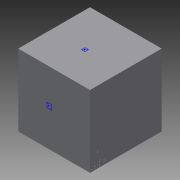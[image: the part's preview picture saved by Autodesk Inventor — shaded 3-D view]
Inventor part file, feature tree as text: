
AUTODESK INVENTOR PART (.ipt)
format: ipt  version: 2014 (Build 180170000, 170)  size: 649,728 bytes
history: native  units: mm
features: sketch x56, extrude x53, other x51
ambient origin geometry x8: Origin, YZ Plane, XZ Plane, XY Plane, X Axis, Y Axis, Z Axis, Center Point
bodies: 实体1 (feature_tree)
feature tree (160):
  extrude  "拉伸1"  Depth=200.0mm
  other  "UCS1"
  other  "UCS2"
  other  "UCS3"
  other  "UCS4"
  other  "UCS5"
  other  "UCS6"
  extrude  "拉伸2"  Depth=43.0mm
  extrude  "拉伸3"  Depth=4.25mm
  extrude  "拉伸4"  Depth=15.5mm
  extrude  "拉伸5"  TaperAngle=0.0deg  [1 undecoded]
  extrude  "拉伸6"  Depth=0.75mm
  extrude  "拉伸7"  Depth=31.75mm
  extrude  "拉伸8"  Depth=18.5mm
  extrude  "拉伸9"  Depth=18.5mm
  extrude  "拉伸10"  Depth=5.0mm
  extrude  "拉伸11"  Depth=16.0mm
  extrude  "拉伸12"  Depth=21.5mm
  extrude  "拉伸13"  Depth=12.7mm
  extrude  "拉伸14"  Depth=21.5mm
  other  "iFeature2:1"
  other  "Footprint1"
  other  "Footprint4"
  extrude  "拉伸15"  Depth=30.2mm
  extrude  "拉伸20"  Depth=21.0mm
  extrude  "拉伸21"  Depth=21.0mm
  extrude  "拉伸22"  Depth=4.0mm
  extrude  "拉伸23"  Depth=33.0mm
  extrude  "拉伸24"  Depth=4.0mm
  extrude  "拉伸25"  TaperAngle=0.0deg  [1 undecoded]
  extrude  "拉伸26"  TaperAngle=0.0deg  [1 undecoded]
  extrude  "拉伸27"  Depth=30.0mm
  extrude  "拉伸28"  Depth=12.0mm
  extrude  "拉伸29"  Depth=10.25mm
  extrude  "拉伸30"  Depth=35.05mm
  extrude  "拉伸31"  Depth=95.0mm
  extrude  "拉伸32"  Depth=50.0mm
  extrude  "拉伸33"  Depth=6.8mm
  extrude  "拉伸36"  Depth=38.1mm
  extrude  "拉伸37"  TaperAngle=0.0deg  [1 undecoded]
  extrude  "拉伸38"  Depth=76.2mm
  extrude  "拉伸39"  Depth=82.6mm
  extrude  "拉伸40"  Depth=26.0mm
  extrude  "拉伸41"  Depth=26.0mm
  extrude  "拉伸42"  Depth=8.0mm
  extrude  "拉伸43"  Depth=22.0mm
  extrude  "拉伸44"  Depth=9.5mm
  extrude  "拉伸45"  Depth=28.0mm
  extrude  "拉伸46"  Depth=12.0mm
  extrude  "拉伸47"  Depth=29.0mm TaperAngle=0.0deg
  extrude  "拉伸48"  Depth=11.1mm
  extrude  "拉伸49"  Depth=38.0mm
  extrude  "拉伸50"  Depth=14.7mm
  extrude  "拉伸51"  Depth=73.8mm
  extrude  "拉伸52"  Depth=31.0mm
  extrude  "拉伸53"  Depth=57.0mm
  extrude  "拉伸54"  Depth=32.0mm TaperAngle=0.0deg
  extrude  "拉伸55"  Depth=7.5mm
  extrude  "拉伸56"  Depth=4.0mm
  extrude  "拉伸57"  Depth=4.0mm
  extrude  "拉伸58"  Depth=4.0mm
  extrude  "拉伸59"  Depth=8.0mm TaperAngle=0.0deg
  sketch  "草图1"  dims[d0=1000.0mm d1=0.0mm]
  sketch  "草图2"  dims[d2=0.0mm d3=0.0mm d4=0.0mm d5=0.0mm d6=0.0mm d7=0.0mm]
  sketch  "草图3"  dims[d8=0.0mm d9=0.0mm d10=0.0mm d11=0.0mm d12=0.0mm d13=0.0mm]
  sketch  "草图4"  dims[d14=0.0mm d15=0.0mm d16=0.0mm d17=0.0mm d18=0.0mm d19=0.0mm]
  sketch  "草图5"  dims[d20=0.0mm d21=0.0mm d22=0.0mm d23=0.0mm d24=0.0mm d25=0.0mm]
  sketch  "草图6"  dims[d26=0.0mm d27=0.0mm d28=0.0mm d29=0.0mm d30=0.0mm d31=0.0mm]
  sketch  "草图7"  dims[d32=0.0mm d33=0.0mm d34=0.0mm d35=0.0mm d36=0.0mm d37=0.0mm d38=200.0mm]
  sketch  "草图8"  dims[d39=100.0mm d40=43.0mm]
  sketch  "草图9"  dims[d41=51.0mm d42=4.25mm]
  sketch  "草图10"  dims[d43=21.5mm d44=15.5mm]
  sketch  "草图11"  dims[d45=31.0mm d46=0.0mm]
  sketch  "草图12"  dims[d47=40.5mm d48=0.75mm]
  sketch  "草图13"  dims[d49=40.5mm d50=31.75mm]
  sketch  "草图14"  dims[d51=18.5mm d52=0.0mm d53=18.5mm d54=-10.297443mm]
  sketch  "草图24"  dims[d67=25.9mm d68=21.5mm]
  sketch  "草图29"  dims[d69=15.5mm d70=12.7mm]
  sketch  "草图30"  dims[d71=5.1mm d72=21.5mm]
  sketch  "草图31"  dims[d73=15.5mm d74=30.2mm]
  sketch  "草图32"  dims[d75=21.0mm d76=0.0mm d77=21.0mm d78=-10.297443mm]
  sketch  "草图33"  dims[d79=21.0mm d80=-10.297443mm d81=21.0mm d82=-10.297443mm]
  sketch  "草图34"  dims[d83=21.0mm d84=-10.297443mm d85=4.0mm]
  sketch  "草图35"  dims[d86=31.75mm d87=33.0mm]
  sketch  "草图36"  dims[d88=4.0mm d89=0.0mm d90=4.0mm d91=-10.297443mm]
  sketch  "草图37"  dims[d105=0.0mm d119=0.0mm]
  sketch  "草图38"  dims[d125=0.0mm d131=0.0mm]
  sketch  "草图39"  dims[d135=0.0mm d139=30.0mm]
  sketch  "草图40"  dims[d140=20.0mm d141=12.0mm]
  sketch  "草图41"  dims[d142=19.05mm d143=0.0mm d153=10.25mm]
  sketch  "草图42"  dims[d154=35.05mm d155=0.0mm d156=35.05mm d157=-10.297443mm]
  sketch  "草图45"  dims[d158=35.05mm d159=-10.297443mm d160=95.0mm]
  sketch  "草图46"  dims[d161=102.0mm d162=50.0mm]
  sketch  "草图47"  dims[d163=100.0mm d167=6.8mm]
  sketch  "草图48"  dims[d168=41.8mm d169=38.1mm]
  sketch  "草图49"  dims[d170=76.2mm d171=0.0mm]
  sketch  "草图50"  dims[d172=82.6mm d173=76.2mm]
  sketch  "草图51"  dims[d174=0.0mm d175=82.6mm]
  sketch  "草图52"  dims[d176=26.0mm d177=0.0mm d178=26.0mm d179=-10.297443mm]
  sketch  "草图55"  dims[d180=26.0mm d181=-10.297443mm d182=26.0mm d183=-10.297443mm]
  sketch  "草图56"  dims[d184=26.0mm d185=-10.297443mm d186=8.0mm]
  sketch  "草图57"  dims[d187=22.0mm d188=0.0mm d189=14.7mm]
  sketch  "草图58"  dims[d190=38.0mm d191=9.5mm]
  sketch  "草图59"  dims[d204=28.0mm d205=0.0mm d206=28.0mm d207=-10.297443mm]
  sketch  "草图60"  dims[d208=6.3mm d209=12.0mm]
  sketch  "草图61"  dims[d210=11.8mm d211=29.0mm d212=0.0mm]
  sketch  "草图62"  dims[d213=29.0mm d214=-10.297443mm d215=11.1mm]
  sketch  "草图63"  dims[d216=46.8mm d217=38.0mm]
  sketch  "草图64"  dims[d218=30.0mm d219=0.0mm d224=14.7mm]
  sketch  "草图65"  dims[d225=19.0mm d226=73.8mm]
  sketch  "草图66"  dims[d227=31.0mm d228=0.0mm d229=31.0mm d230=-10.297443mm]
  sketch  "草图67"  dims[d231=14.7mm d232=57.0mm]
  sketch  "草图68"  dims[d233=73.8mm d234=32.0mm d235=0.0mm]
  sketch  "草图69"  dims[d236=32.0mm d237=-10.297443mm d238=7.5mm]
  sketch  "草图70"  dims[d239=3.2mm d240=23.8mm d241=79.4mm d242=23.8mm d243=8.0mm d244=0.0mm d245=8.0mm d246=-10.297443mm d247=8.0mm d248=-10.297443mm d249=8.0mm d250=-10.297443mm d267=43.0mm d268=51.0mm d269=50.0mm d270=200.0mm d271=21.5mm d272=15.5mm d273=4.25mm d274=0.75mm d275=40.5mm d276=40.5mm d277=31.75mm d278=0.0mm d279=31.0mm d280=18.5mm d281=0.0mm d282=18.5mm d283=-10.297443mm d284=18.5mm d285=-10.297443mm d286=18.5mm d287=-10.297443mm d288=18.5mm d289=-10.297443mm d290=5.0mm d291=16.0mm d292=0.0mm d293=7.5mm d294=21.5mm d295=5.1mm d296=21.0mm d297=0.0mm d298=21.0mm d299=-10.297443mm d300=7.5mm d301=12.7mm d302=15.5mm d303=19.0mm d304=0.0mm d305=19.0mm d306=-10.297443mm d307=7.5mm d308=15.5mm d309=30.2mm d310=20.0mm d311=0.0mm d312=20.0mm d313=-10.297443mm d314=7.5mm d315=25.9mm d316=21.5mm d317=18.0mm d318=0.0mm d319=18.0mm d320=-10.297443mm d321=4.0mm d322=33.0mm d323=31.75mm d324=4.0mm d325=0.0mm d326=4.0mm d327=-10.297443mm]
  other  "UCS1: YZ 平面"
  other  "UCS1: XZ 平面"
  other  "UCS1: XY 平面"
  other  "UCS1: X 轴"
  other  "UCS1: Y 轴"
  other  "UCS1: Z 轴"
  other  "UCS1: 原点"
  other  "UCS2: YZ 平面"
  other  "UCS2: XZ 平面"
  other  "UCS2: XY 平面"
  other  "UCS2: X 轴"
  other  "UCS2: Y 轴"
  other  "UCS2: Z 轴"
  other  "UCS2: 原点"
  other  "UCS3: YZ 平面"
  other  "UCS3: XZ 平面"
  other  "UCS3: XY 平面"
  other  "UCS3: X 轴"
  other  "UCS3: Y 轴"
  other  "UCS3: Z 轴"
  other  "UCS3: 原点"
  other  "UCS4: YZ 平面"
  other  "UCS4: XZ 平面"
  other  "UCS4: XY 平面"
  other  "UCS4: X 轴"
  other  "UCS4: Y 轴"
  other  "UCS4: Z 轴"
  other  "UCS4: 原点"
  other  "UCS5: YZ 平面"
  other  "UCS5: XZ 平面"
  other  "UCS5: XY 平面"
  other  "UCS5: X 轴"
  other  "UCS5: Y 轴"
  other  "UCS5: Z 轴"
  other  "UCS5: 原点"
  other  "UCS6: YZ 平面"
  other  "UCS6: XZ 平面"
  other  "UCS6: XY 平面"
  other  "UCS6: X 轴"
  other  "UCS6: Y 轴"
  other  "UCS6: Z 轴"
  other  "UCS6: 原点"
  sketch  "草图15"  dims[d55=18.5mm d56=-10.297443mm d57=18.5mm d58=-10.297443mm]
  sketch  "草图16"  dims[d59=18.5mm d60=-10.297443mm d61=5.0mm]
  sketch  "草图18"  dims[d62=16.0mm d63=0.0mm d64=7.5mm]
note: 4 required parameter values undecoded (feature->parameter linkage not recoverable at this tier; creation-order binding heuristic only, values carry confidence <= 0.55)
